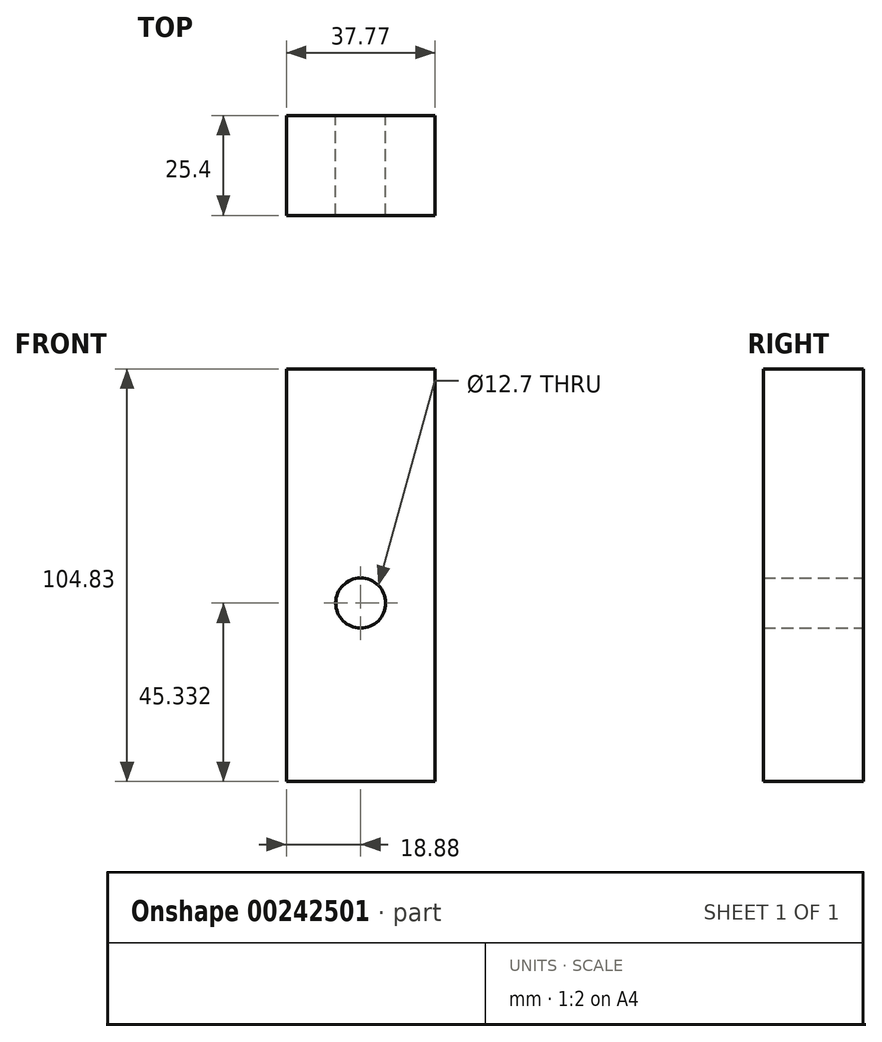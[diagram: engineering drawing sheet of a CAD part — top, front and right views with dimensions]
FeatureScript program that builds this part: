
annotation { "Feature Type Name" : "Feature", "Feature Type Description" : "" }
export const myFeature = defineFeature(function(context is Context, id is Id, definition is map)
    precondition{}
    {
        {
            var Q0;
            Q0=qCreatedBy(makeId("Front.planeOp"),FACE);
            var sketch = newSketch(context, id + "F0", { "sketchPlane" : qUnion([Q0])});
            skLineSegment(sketch, "E0.bottom", {"start": v(44.33, -39.78) * mm, "end": v(6.56, -39.78) * mm});
            skLineSegment(sketch, "E0.top", {"start": v(44.33, 65.05) * mm, "end": v(6.56, 65.05) * mm});
            skLineSegment(sketch, "E0.left", {"start": v(44.33, -39.78) * mm, "end": v(44.33, 65.05) * mm});
            skLineSegment(sketch, "E0.right", {"start": v(6.56, -39.78) * mm, "end": v(6.56, 65.05) * mm});
            skSolve(sketch);
        }
        {
            var Q0;
            Q0 = qSketchRegion(id + "F0", true);
            extrude(context, id + "F1", {"entities" : qUnion([Q0]), "depth" : 25.4 * mm});
        }
        {
            var Q0;
            Q0=makeQuery(id+"F1.opExtrude","CAP_FACE",FACE,{"disambiguationData":[OSD([sQuery(id+"F0.wireOp",EDGE,"E0.bottom"),sQuery(id+"F0.wireOp",EDGE,"E0.top"),sQuery(id+"F0.wireOp",EDGE,"E0.left"),sQuery(id+"F0.wireOp",EDGE,"E0.right")])],"isStart":true});
            var sketch = newSketch(context, id + "F2", { "sketchPlane" : qUnion([Q0])});
            skCircle(sketch, "E1", {"center": v(-25.44, 5.55) * mm, "radius": 6.77 * mm});
            skSolve(sketch);
        }
        {
            var Q0;
            Q0=sQuery(id+"F2.wireOp",VERTEX,"E1.center");
            var Q1;
            Q1=makeQuery(id+"F1.opExtrude","SWEPT_BODY",BODY,{"disambiguationData":[OSD([sQuery(id+"F0.wireOp",EDGE,"E0.bottom"),sQuery(id+"F0.wireOp",EDGE,"E0.top"),sQuery(id+"F0.wireOp",EDGE,"E0.left"),sQuery(id+"F0.wireOp",EDGE,"E0.right")])]});
            hole(context, id + "F3", {"style" : HoleStyle.SIMPLE, "endStyle" : HoleEndStyle.THROUGH, "holeDiameter" : 12.7 * mm, "locations" : qUnion([Q0]), "scope" : qUnion([Q1]), "isTappedThrough" : true});
        }
    });
